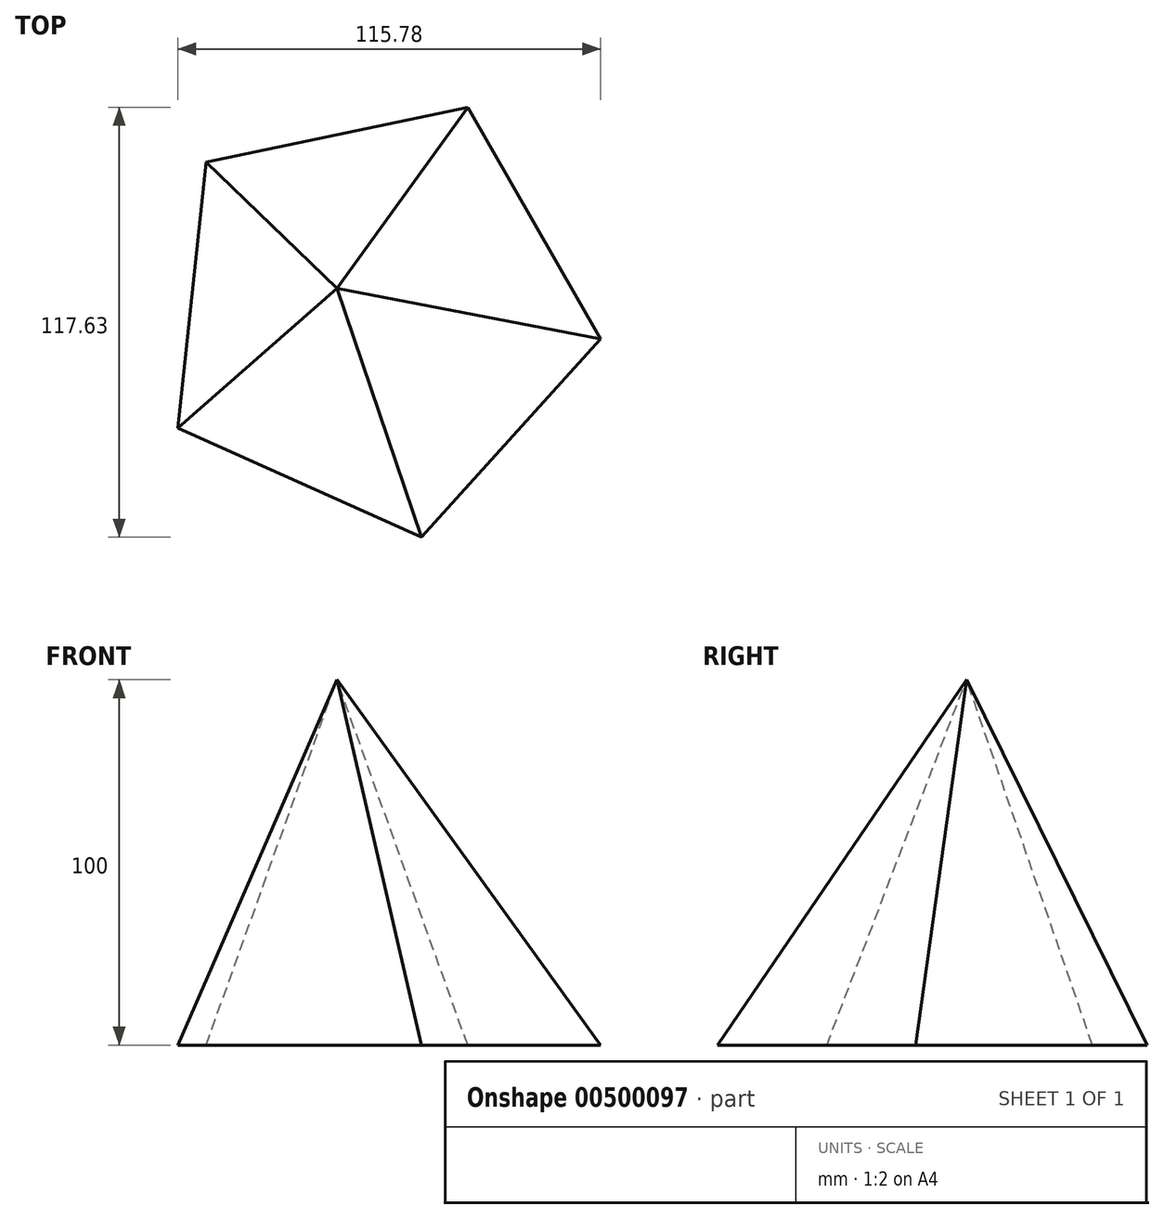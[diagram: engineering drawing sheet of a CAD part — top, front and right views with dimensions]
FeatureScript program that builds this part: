
annotation { "Feature Type Name" : "Feature", "Feature Type Description" : "" }
export const myFeature = defineFeature(function(context is Context, id is Id, definition is map)
    precondition{}
    {
        {
            var Q0;
            Q0=qCreatedBy(makeId("Top.planeOp"),FACE);
            var sketch = newSketch(context, id + "F0", { "sketchPlane" : qUnion([Q0])});
            skCircle(sketch, "E0.cCircle", {"center": v(0, 0) * mm, "radius": 62.2 * mm, "construction": true});
            skLineSegment(sketch, "E0.0", {"start": v(-46.13, 41.72) * mm, "end": v(25.43, 56.76) * mm});
            skLineSegment(sketch, "E0.1", {"start": v(25.43, 56.76) * mm, "end": v(61.84, -6.64) * mm});
            skLineSegment(sketch, "E0.2", {"start": v(61.84, -6.64) * mm, "end": v(12.8, -60.87) * mm});
            skLineSegment(sketch, "E0.3", {"start": v(12.8, -60.87) * mm, "end": v(-53.94, -30.98) * mm});
            skLineSegment(sketch, "E0.4", {"start": v(-53.94, -30.98) * mm, "end": v(-46.13, 41.72) * mm});
            skSolve(sketch);
        }
        {
            var Q0;
            Q0=qCreatedBy(makeId("Top.planeOp"),FACE);
            cPlane(context, id + "F1", {"entities" : qUnion([Q0]), "cplaneType" : CPlaneType.OFFSET, "offset" : 100 * mm, "width" : 150 * mm, "height" : 150 * mm});
        }
        {
            var Q0;
            Q0=qCreatedBy(id+"F1.planeOp",FACE);
            var sketch = newSketch(context, id + "F2", { "sketchPlane" : qUnion([Q0])});
            skPoint(sketch, "E1", {"position": v(-10.37, 7.28) * mm});
            skSolve(sketch);
        }
        {
            var Q0;
            Q0=makeQuery(id+"F0.imprint","IMPRINT",FACE,{"disambiguationData":[TD([[makeQuery(id+"F0.imprint","IMPRINT",EDGE,{"derivedFrom":sQuery(id+"F0.wireOp",EDGE,"E0.0")}),-1.0]])]});
            var Q1;
            Q1=sQuery(id+"F2.wireOp",VERTEX,"E1");
            loft(context, id + "F3", {"sheetProfilesArray" : [{ "sheetProfileEntities" : qUnion([Q0]) }, { "sheetProfileEntities" : qUnion([Q1]) }]});
        }
    });
